# Revit family: Sensor-Lutron-Vive_PowPak_Sensor_Fixture
name_source: partatom
category: Lighting Devices
revit_build: Autodesk Revit 2017 (Build: 20160720_1515(x64)
units: mm (PartAtom-declared; Revit-internal decimal feet)

## family parameters
Cut with Voids When Loaded = No
Host = Face
Maintain Annotation Orientation = No
OmniClass Number = 23.85.80.11.27
OmniClass Title = Lighting Controls
Part Type = Normal
Room Calculation Point = No
Round Connector Dimension = Use Radius
Shared = No

## types (2) — shared parameters
Assembly Code = D5030800
Base Cover Flange Angle = 156.80°
Cover Gap = 0' - 0 1/32"
Current = 25 mA
Default Elevation = 0' - 0"
Description = PowPak Fixture Sensor
Field of View = 360.00°
Instruction Sheet Link = http://www.lutron.com
Light Level = 150 fc
Major Motion Coverage Radius = 9' - 9 19/32"
Manufacturer = Lutron Electronics Co., Inc
Manufacturer Fax Number = 610-282-1243
Maximum Coverage = 300.00 SF
Maximum Operating Temperature = 104 °F
Minimum Coverage = 150.00 SF
Minimum Operating Temperature = 32 °F
Minor Motion Coverage Radius = 6' - 10 13/16"
Overall Depth = 0' - 1 1/2"
Overall Width = 0' - 0 21/32"
Performance URL = http://www.lutron.com
Product Documentation Link = http://www.lutron.com
Product Name = PowPak Fixture Sensor
Product Page URL = http://www.lutron.com
Sensor Body Radius = 0' - 0 3/4"
Sensor Material = Plastic - Lutron - White
Sensor Sphere Diameter = 0' - 0 1/2"
Sensor Sphere Offset = 0' - 0 1/8"
Sensor Sphere Radius = 0' - 0 1/4"
Series = Vive
Top Cover Flange Angle = 170.61°
Top Cover Side Flange Angle = 80.00°
URL = http://www.lutron.com
Version = 2017 - v1.0b
Video Link = https://www.youtube.com
Voltage = 12 V
Warranty URL = http://www.lutron.com
zero-valued in all types: Cost

## per-type parameters (varying)
| type | Label |
| FC-SENSOR | FS |
| FC-VSENSOR | VS |

note: column(s) folded — value = type name in every type: Model

## geometry (parser evidence)
native form markers: Blend x10, Sweep x6
no freeform markers — native parametric forms only
